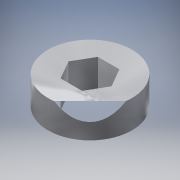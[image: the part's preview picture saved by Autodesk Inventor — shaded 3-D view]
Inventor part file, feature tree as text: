
AUTODESK INVENTOR PART (.ipt)
format: ipt  version: 2016 (Build 200138000, 138)  size: 104,448 bytes
history: native  units: in
note: dims shown in document units (in); Inventor stores cm internally (conversion verified against a paired STEP export)
features: extrude x1, sketch x1
ambient origin geometry x8: Origin, YZ Plane, XZ Plane, XY Plane, X Axis, Y Axis, Z Axis, Center Point
bodies: Solid1 (feature_tree)
feature tree (2):
  extrude  "Extrusion1"  Depth=0.5in
  sketch  "Sketch1"  dims[d0=1.125in d1=0.5in d2=0.375in d3=0.0in]
